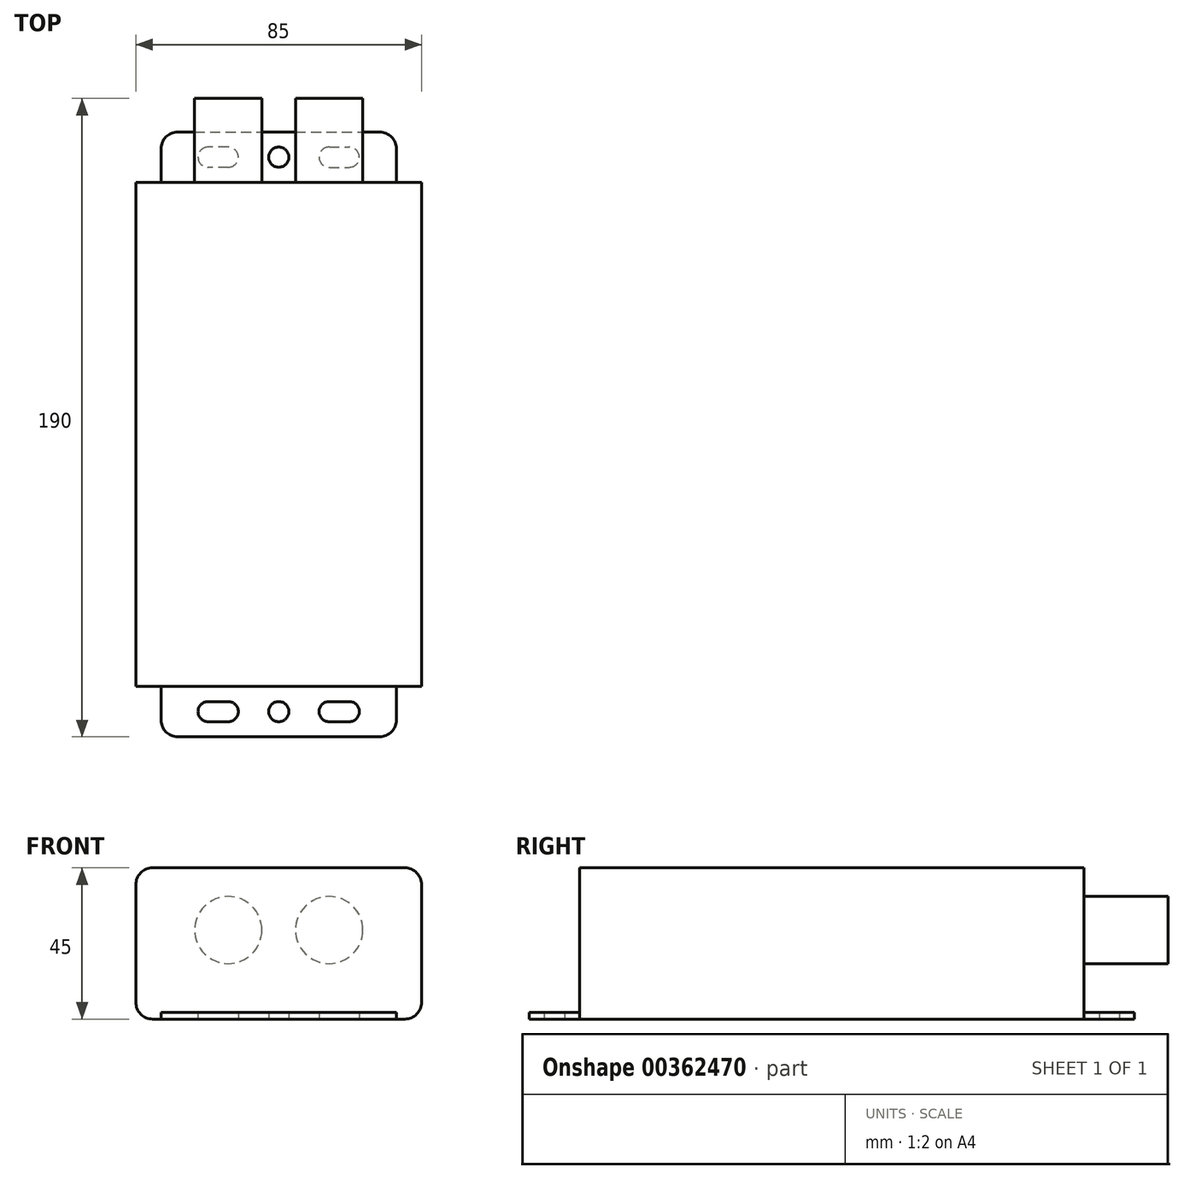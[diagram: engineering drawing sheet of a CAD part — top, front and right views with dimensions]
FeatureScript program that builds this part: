
annotation { "Feature Type Name" : "Feature", "Feature Type Description" : "" }
export const myFeature = defineFeature(function(context is Context, id is Id, definition is map)
    precondition{}
    {
        {
            var Q0;
            Q0=qCreatedBy(makeId("Front.planeOp"),FACE);
            var sketch = newSketch(context, id + "F0", { "sketchPlane" : qUnion([Q0])});
            skLineSegment(sketch, "E0.bottom", {"start": v(37.5, 22.5) * mm, "end": v(-37.5, 22.5) * mm});
            skLineSegment(sketch, "E0.top", {"start": v(37.5, -22.5) * mm, "end": v(-37.5, -22.5) * mm});
            skLineSegment(sketch, "E0.left", {"start": v(42.5, 17.5) * mm, "end": v(42.5, -17.5) * mm});
            skLineSegment(sketch, "E0.right", {"start": v(-42.5, 17.5) * mm, "end": v(-42.5, -17.5) * mm});
            skPoint(sketch, "E0.middle", {"position": v(0, 0) * mm});
            skPoint(sketch, "E1.visualSharp", {"position": v(-42.5, 22.5) * mm});
            skArc(sketch, "E1.filletArc", {"start": v(-37.5, 22.5) * mm, "mid": v(-41.04, 21.04) * mm, "end": v(-42.5, 17.5) * mm});
            skPoint(sketch, "E2.visualSharp", {"position": v(-42.5, -22.5) * mm});
            skArc(sketch, "E2.filletArc", {"start": v(-42.5, -17.5) * mm, "mid": v(-41.04, -21.04) * mm, "end": v(-37.5, -22.5) * mm});
            skPoint(sketch, "E3.visualSharp", {"position": v(42.5, -22.5) * mm});
            skArc(sketch, "E3.filletArc", {"start": v(37.5, -22.5) * mm, "mid": v(41.04, -21.04) * mm, "end": v(42.5, -17.5) * mm});
            skPoint(sketch, "E4.visualSharp", {"position": v(42.5, 22.5) * mm});
            skArc(sketch, "E4.filletArc", {"start": v(42.5, 17.5) * mm, "mid": v(41.04, 21.04) * mm, "end": v(37.5, 22.5) * mm});
            skSolve(sketch);
        }
        {
            var Q0;
            Q0 = qSketchRegion(id + "F0", true);
            extrude(context, id + "F1", {"entities" : qUnion([Q0]), "depth" : 150 * mm, "offsetDistance" : 25 * mm});
        }
        {
            var Q0;
            Q0=makeQuery(id+"F1.opExtrude","SWEPT_FACE",FACE,{"disambiguationData":[OSD([sQuery(id+"F0.wireOp",EDGE,"E0.top")])]});
            var sketch = newSketch(context, id + "F2", { "sketchPlane" : qUnion([Q0])});
            skLineSegment(sketch, "E5.bottom", {"start": v(-30, 165) * mm, "end": v(30, 165) * mm});
            skLineSegment(sketch, "E5.top", {"start": v(-30, -15) * mm, "end": v(30, -15) * mm});
            skLineSegment(sketch, "E5.left", {"start": v(-35, 160) * mm, "end": v(-35, -10) * mm});
            skLineSegment(sketch, "E5.right", {"start": v(35, 160) * mm, "end": v(35, -10) * mm});
            skPoint(sketch, "E5.middle", {"position": v(0, 75) * mm});
            skPoint(sketch, "E6.visualSharp", {"position": v(-35, 165) * mm});
            skArc(sketch, "E6.filletArc", {"start": v(-30, 165) * mm, "mid": v(-33.54, 163.54) * mm, "end": v(-35, 160) * mm});
            skPoint(sketch, "E7.visualSharp", {"position": v(35, 165) * mm});
            skArc(sketch, "E7.filletArc", {"start": v(35, 160) * mm, "mid": v(33.54, 163.54) * mm, "end": v(30, 165) * mm});
            skPoint(sketch, "E8.visualSharp", {"position": v(35, -15) * mm});
            skArc(sketch, "E8.filletArc", {"start": v(30, -15) * mm, "mid": v(33.54, -13.54) * mm, "end": v(35, -10) * mm});
            skPoint(sketch, "E9.visualSharp", {"position": v(-35, -15) * mm});
            skArc(sketch, "E9.filletArc", {"start": v(-35, -10) * mm, "mid": v(-33.54, -13.54) * mm, "end": v(-30, -15) * mm});
            skLineSegment(sketch, "E10", {"start": v(-35, 75) * mm, "end": v(35, 75) * mm, "construction": true});
            skCircle(sketch, "E11", {"center": v(0, 157.5) * mm, "radius": 3 * mm});
            skLineSegment(sketch, "E12", {"start": v(-35, 157.5) * mm, "end": v(35, 157.5) * mm, "construction": true});
            skLineSegment(sketch, "E13.bottom", {"start": v(-15, 160.5) * mm, "end": v(-21, 160.5) * mm});
            skLineSegment(sketch, "E13.top", {"start": v(-15, 154.5) * mm, "end": v(-21, 154.5) * mm});
            skLineSegment(sketch, "E13.left", {"start": v(-12, 157.5) * mm, "end": v(-12, 157.5) * mm});
            skLineSegment(sketch, "E13.right", {"start": v(-24, 157.5) * mm, "end": v(-24, 157.5) * mm});
            skPoint(sketch, "E13.middle", {"position": v(-18, 157.5) * mm});
            skPoint(sketch, "E14.visualSharp", {"position": v(-24, 160.5) * mm});
            skArc(sketch, "E14.filletArc", {"start": v(-21, 160.5) * mm, "mid": v(-23.12, 159.62) * mm, "end": v(-24, 157.5) * mm});
            skPoint(sketch, "E15.visualSharp", {"position": v(-24, 154.5) * mm});
            skArc(sketch, "E15.filletArc", {"start": v(-24, 157.5) * mm, "mid": v(-23.12, 155.38) * mm, "end": v(-21, 154.5) * mm});
            skPoint(sketch, "E16.visualSharp", {"position": v(-12, 154.5) * mm});
            skArc(sketch, "E16.filletArc", {"start": v(-15, 154.5) * mm, "mid": v(-12.88, 155.38) * mm, "end": v(-12, 157.5) * mm});
            skPoint(sketch, "E17.visualSharp", {"position": v(-12, 160.5) * mm});
            skArc(sketch, "E17.filletArc", {"start": v(-12, 157.5) * mm, "mid": v(-12.88, 159.62) * mm, "end": v(-15, 160.5) * mm});
            skLineSegment(sketch, "E18.MirrorCS", {"start": v(15, 160.5) * mm, "end": v(21, 160.5) * mm});
            skLineSegment(sketch, "E19.MirrorCS", {"start": v(24, 157.5) * mm, "end": v(24, 157.5) * mm});
            skPoint(sketch, "E20.MirrorP", {"position": v(24, 160.5) * mm});
            skArc(sketch, "E21.MirrorCS", {"start": v(21, 160.5) * mm, "mid": v(23.12, 159.62) * mm, "end": v(24, 157.5) * mm});
            skPoint(sketch, "E22.MirrorP", {"position": v(18, 157.5) * mm});
            skArc(sketch, "E23.MirrorCS", {"start": v(15, 154.5) * mm, "mid": v(12.88, 155.38) * mm, "end": v(12, 157.5) * mm});
            skArc(sketch, "E24.MirrorCS", {"start": v(24, 157.5) * mm, "mid": v(23.12, 155.38) * mm, "end": v(21, 154.5) * mm});
            skLineSegment(sketch, "E25.MirrorCS", {"start": v(15, 154.5) * mm, "end": v(21, 154.5) * mm});
            skArc(sketch, "E26.MirrorCS", {"start": v(12, 157.5) * mm, "mid": v(12.88, 159.62) * mm, "end": v(15, 160.5) * mm});
            skPoint(sketch, "E27.MirrorP", {"position": v(12, 160.5) * mm});
            skPoint(sketch, "E28.MirrorP", {"position": v(12, 154.5) * mm});
            skPoint(sketch, "E29.MirrorP", {"position": v(24, 154.5) * mm});
            skLineSegment(sketch, "E30.MirrorCS", {"start": v(12, 157.5) * mm, "end": v(12, 157.5) * mm});
            skArc(sketch, "E31.MirrorCS", {"start": v(21, -10.5) * mm, "mid": v(23.12, -9.62) * mm, "end": v(24, -7.5) * mm});
            skArc(sketch, "E32.MirrorCS", {"start": v(-15, -4.5) * mm, "mid": v(-12.88, -5.38) * mm, "end": v(-12, -7.5) * mm});
            skArc(sketch, "E33.MirrorCS", {"start": v(24, -7.5) * mm, "mid": v(23.12, -5.38) * mm, "end": v(21, -4.5) * mm});
            skArc(sketch, "E34.MirrorCS", {"start": v(15, -4.5) * mm, "mid": v(12.88, -5.38) * mm, "end": v(12, -7.5) * mm});
            skPoint(sketch, "E35.MirrorP", {"position": v(24, -10.5) * mm});
            skLineSegment(sketch, "E36.MirrorCS", {"start": v(15, -10.5) * mm, "end": v(21, -10.5) * mm});
            skArc(sketch, "E37.MirrorCS", {"start": v(-21, -10.5) * mm, "mid": v(-23.12, -9.62) * mm, "end": v(-24, -7.5) * mm});
            skArc(sketch, "E38.MirrorCS", {"start": v(12, -7.5) * mm, "mid": v(12.88, -9.62) * mm, "end": v(15, -10.5) * mm});
            skArc(sketch, "E39.MirrorCS", {"start": v(-24, -7.5) * mm, "mid": v(-23.12, -5.38) * mm, "end": v(-21, -4.5) * mm});
            skArc(sketch, "E40.MirrorCS", {"start": v(-12, -7.5) * mm, "mid": v(-12.88, -9.62) * mm, "end": v(-15, -10.5) * mm});
            skLineSegment(sketch, "E41.MirrorCS", {"start": v(24, -7.5) * mm, "end": v(24, -7.5) * mm});
            skPoint(sketch, "E42.MirrorP", {"position": v(18, -7.5) * mm});
            skPoint(sketch, "E43.MirrorP", {"position": v(-24, -4.5) * mm});
            skPoint(sketch, "E44.MirrorP", {"position": v(12, -4.5) * mm});
            skPoint(sketch, "E45.MirrorP", {"position": v(-18, -7.5) * mm});
            skLineSegment(sketch, "E46.MirrorCS", {"start": v(12, -7.5) * mm, "end": v(12, -7.5) * mm});
            skLineSegment(sketch, "E47.MirrorCS", {"start": v(-15, -4.5) * mm, "end": v(-21, -4.5) * mm});
            skLineSegment(sketch, "E48.MirrorCS", {"start": v(-12, -7.5) * mm, "end": v(-12, -7.5) * mm});
            skPoint(sketch, "E49.MirrorP", {"position": v(-12, -4.5) * mm});
            skPoint(sketch, "E50.MirrorP", {"position": v(12, -10.5) * mm});
            skPoint(sketch, "E51.MirrorP", {"position": v(-12, -10.5) * mm});
            skLineSegment(sketch, "E52.MirrorCS", {"start": v(15, -4.5) * mm, "end": v(21, -4.5) * mm});
            skLineSegment(sketch, "E53.MirrorCS", {"start": v(-24, -7.5) * mm, "end": v(-24, -7.5) * mm});
            skPoint(sketch, "E54.MirrorP", {"position": v(24, -4.5) * mm});
            skLineSegment(sketch, "E55.MirrorCS", {"start": v(-15, -10.5) * mm, "end": v(-21, -10.5) * mm});
            skPoint(sketch, "E56.MirrorP", {"position": v(-24, -10.5) * mm});
            skCircle(sketch, "E57.MirrorC", {"center": v(0, -7.5) * mm, "radius": 3 * mm});
            skSolve(sketch);
        }
        {
            var Q0;
            Q0 = qSketchRegion(id + "F2", true);
            extrude(context, id + "F3", {"entities" : qUnion([Q0]), "operationType" : NewBodyOperationType.ADD, "oppositeDirection" : true, "depth" : 2 * mm, "offsetDistance" : 25 * mm});
        }
        {
            var Q0;
            Q0=qCreatedBy(makeId("Front.planeOp"),FACE);
            var sketch = newSketch(context, id + "F4", { "sketchPlane" : qUnion([Q0])});
            skLineSegment(sketch, "E58", {"start": v(42.5, 4) * mm, "end": v(-42.5, 4) * mm, "construction": true});
            skCircle(sketch, "E59", {"center": v(15, 4) * mm, "radius": 10 * mm});
            skCircle(sketch, "E60", {"center": v(-15, 4) * mm, "radius": 10 * mm});
            skSolve(sketch);
        }
        {
            var Q0;
            Q0 = qSketchRegion(id + "F4", true);
            extrude(context, id + "F5", {"entities" : qUnion([Q0]), "operationType" : NewBodyOperationType.ADD, "oppositeDirection" : true, "depth" : 25 * mm, "offsetDistance" : 25 * mm});
        }
    });
